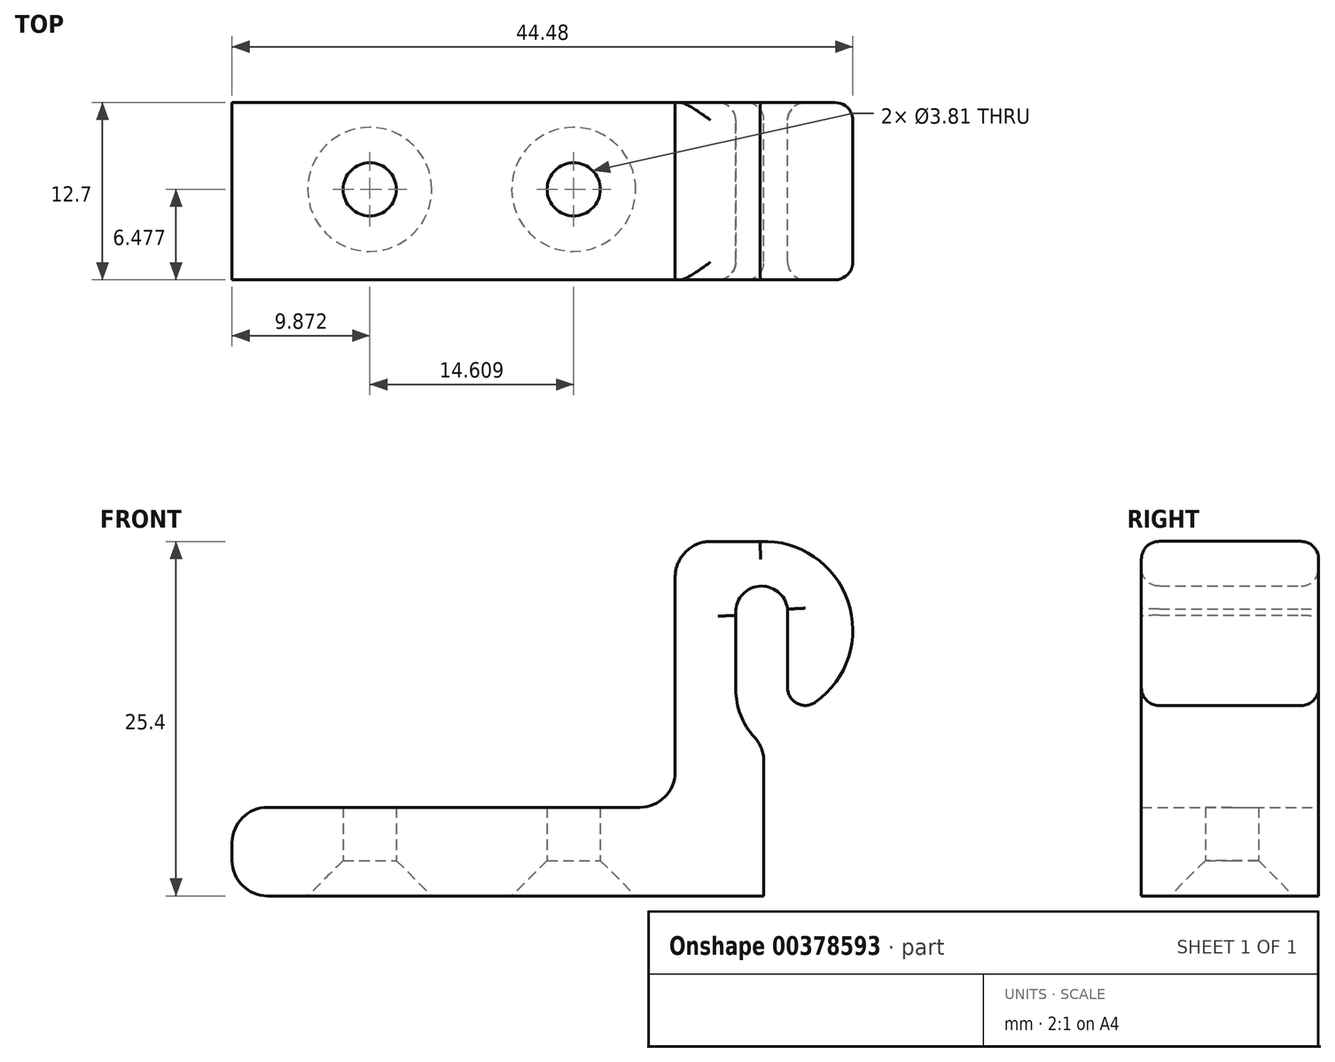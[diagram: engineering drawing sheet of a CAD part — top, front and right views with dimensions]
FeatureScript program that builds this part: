
annotation { "Feature Type Name" : "Feature", "Feature Type Description" : "" }
export const myFeature = defineFeature(function(context is Context, id is Id, definition is map)
    precondition{}
    {
        {
            var Q0;
            Q0=qCreatedBy(makeId("Front.planeOp"),FACE);
            var sketch = newSketch(context, id + "F0", { "sketchPlane" : qUnion([Q0])});
            skLineSegment(sketch, "E0.bottom", {"start": v(-17.17, 1.34) * mm, "end": v(14.58, 1.34) * mm});
            skLineSegment(sketch, "E0.top", {"start": v(-17.17, -5.01) * mm, "end": v(20.93, -5.01) * mm});
            skLineSegment(sketch, "E0.left", {"start": v(-17.17, 1.34) * mm, "end": v(-17.17, -5.01) * mm});
            skLineSegment(sketch, "E0.right", {"start": v(20.93, 1.34) * mm, "end": v(20.93, -5.01) * mm});
            skLineSegment(sketch, "E1.bottom", {"start": v(14.58, 20.39) * mm, "end": v(20.93, 20.39) * mm});
            skLineSegment(sketch, "E1.top", {"start": v(14.58, -5.01) * mm, "end": v(20.93, -5.01) * mm});
            skLineSegment(sketch, "E1.left", {"start": v(14.58, 20.39) * mm, "end": v(14.58, 1.34) * mm});
            skLineSegment(sketch, "E1.right", {"start": v(20.93, 7.13) * mm, "end": v(20.93, -5.01) * mm});
            skArc(sketch, "E2", {"start": v(22.64, 7.92) * mm, "mid": v(27.23, 15.03) * mm, "end": v(20.67, 20.39) * mm});
            skLineSegment(sketch, "E3", {"start": v(22.64, 7.92) * mm, "end": v(22.64, 15.54) * mm});
            skLineSegment(sketch, "E4", {"start": v(18.92, 15.1) * mm, "end": v(18.92, 7.13) * mm});
            skLineSegment(sketch, "E5", {"start": v(18.92, 7.13) * mm, "end": v(20.96, 7.13) * mm});
            skArc(sketch, "E6", {"start": v(22.64, 15.54) * mm, "mid": v(20.56, 17.18) * mm, "end": v(18.92, 15.1) * mm});
            skSolve(sketch);
        }
        {
            var Q0;
            Q0=makeQuery(id+"F0.imprint","IMPRINT",FACE,{"disambiguationData":[TD([[makeQuery(id+"F0.imprint","IMPRINT",EDGE,{"derivedFrom":sQuery(id+"F0.wireOp",EDGE,"E0.bottom")}),-1.0]])]});
            extrude(context, id + "F1", {"entities" : qUnion([Q0]), "depth" : 12.7 * mm});
        }
        {
            var Q0;
            Q0=makeQuery(id+"F1.opExtrude","SWEPT_EDGE",EDGE,{"disambiguationData":[OSD([sQuery(id+"F0.wireOp",EDGE,"E0.bottom"),sQuery(id+"F0.wireOp",EDGE,"E1.left")])]});
            var Q1;
            Q1=makeQuery(id+"F1.opExtrude","SWEPT_EDGE",EDGE,{"disambiguationData":[OSD([sQuery(id+"F0.wireOp",EDGE,"E1.top"),sQuery(id+"F0.wireOp",EDGE,"E1.right")])]});
            var Q2;
            Q2=makeQuery(id+"F1.opExtrude","SWEPT_EDGE",EDGE,{"disambiguationData":[OSD([sQuery(id+"F0.wireOp",EDGE,"E0.bottom"),sQuery(id+"F0.wireOp",EDGE,"E0.left")])]});
            var Q3;
            Q3=makeQuery(id+"F1.opExtrude","SWEPT_EDGE",EDGE,{"disambiguationData":[OSD([sQuery(id+"F0.wireOp",EDGE,"E0.top"),sQuery(id+"F0.wireOp",EDGE,"E0.left")])]});
            var Q4;
            Q4=makeQuery(id+"F1.opExtrude","SWEPT_EDGE",EDGE,{"disambiguationData":[OSD([sQuery(id+"F0.wireOp",EDGE,"E1.bottom"),sQuery(id+"F0.wireOp",EDGE,"E1.left")])]});
            var Q5;
            Q5=makeQuery(id+"F1.opExtrude","SWEPT_EDGE",EDGE,{"disambiguationData":[OSD([sQuery(id+"F0.wireOp",EDGE,"E1.right"),sQuery(id+"F0.wireOp",EDGE,"E5")])]});
            fillet(context, id + "F2", {"entities" : qUnion([Q0, Q1, Q2, Q3, Q4, Q5]), "radius" : 2.54 * mm, "tangentPropagation" : true, "allowEdgeOverflow" : false});
        }
        {
            var Q0;
            Q0=makeQuery(id+"F2.opFillet","BLEND_EDGE",EDGE,{"blendedFrom":[makeQuery(id+"F1.opExtrude","SWEPT_EDGE",EDGE,{"disambiguationData":[OSD([sQuery(id+"F0.wireOp",EDGE,"E1.right"),sQuery(id+"F0.wireOp",EDGE,"E5")])]}),makeQuery(id+"F1.opExtrude","SWEPT_FACE",FACE,{"disambiguationData":[OSD([sQuery(id+"F0.wireOp",EDGE,"E4")])]})],"blendedInto":[makeQuery(id+"F1.opExtrude","SWEPT_FACE",FACE,{"disambiguationData":[OSD([sQuery(id+"F0.wireOp",EDGE,"E4")])]})]});
            fillet(context, id + "F3", {"entities" : qUnion([Q0]), "radius" : 5.08 * mm, "tangentPropagation" : true, "allowEdgeOverflow" : false});
        }
        {
            var Q0;
            Q0=makeQuery(id+"F1.opExtrude","SWEPT_EDGE",EDGE,{"disambiguationData":[OSD([sQuery(id+"F0.wireOp",EDGE,"E2"),sQuery(id+"F0.wireOp",EDGE,"E3")])]});
            fillet(context, id + "F4", {"entities" : qUnion([Q0]), "radius" : 1.27 * mm, "tangentPropagation" : true, "allowEdgeOverflow" : false});
        }
        {
            var Q0;
            Q0=makeQuery(id+"F1.opExtrude","CAP_EDGE",EDGE,{"disambiguationData":[OSD([sQuery(id+"F0.wireOp",EDGE,"E6")])],"isStart":false});
            var Q1;
            Q1=makeQuery(id+"F1.opExtrude","CAP_EDGE",EDGE,{"disambiguationData":[OSD([sQuery(id+"F0.wireOp",EDGE,"E4")])],"isStart":false});
            var Q2;
            {var subQ0=sQuery(id+"F0.wireOp",EDGE,"E3");var subQ1=sQuery(id+"F0.wireOp",EDGE,"E2");Q2=makeQuery(id+"F4.opFillet","BLEND_EDGE",EDGE,{"blendedFrom":[makeQuery(id+"F1.opExtrude","SWEPT_EDGE",EDGE,{"disambiguationData":[OSD([subQ1,subQ0])]}),makeQuery(id+"F1.opExtrude","CAP_FACE",FACE,{"disambiguationData":[OSD([sQuery(id+"F0.wireOp",EDGE,"E0.bottom"),sQuery(id+"F0.wireOp",EDGE,"E0.top"),sQuery(id+"F0.wireOp",EDGE,"E0.left"),sQuery(id+"F0.wireOp",EDGE,"E1.bottom"),sQuery(id+"F0.wireOp",EDGE,"E1.top"),sQuery(id+"F0.wireOp",EDGE,"E1.left"),sQuery(id+"F0.wireOp",EDGE,"E1.right"),subQ1,subQ0,sQuery(id+"F0.wireOp",EDGE,"E4"),sQuery(id+"F0.wireOp",EDGE,"E5"),sQuery(id+"F0.wireOp",EDGE,"E6")])],"isStart":false})],"blendedInto":[makeQuery(id+"F1.opExtrude","CAP_FACE",FACE,{"disambiguationData":[OSD([sQuery(id+"F0.wireOp",EDGE,"E0.bottom"),sQuery(id+"F0.wireOp",EDGE,"E0.top"),sQuery(id+"F0.wireOp",EDGE,"E0.left"),sQuery(id+"F0.wireOp",EDGE,"E1.bottom"),sQuery(id+"F0.wireOp",EDGE,"E1.top"),sQuery(id+"F0.wireOp",EDGE,"E1.left"),sQuery(id+"F0.wireOp",EDGE,"E1.right"),subQ1,subQ0,sQuery(id+"F0.wireOp",EDGE,"E4"),sQuery(id+"F0.wireOp",EDGE,"E5"),sQuery(id+"F0.wireOp",EDGE,"E6")])],"isStart":false})]});}
            var Q3;
            Q3=makeQuery(id+"F1.opExtrude","CAP_EDGE",EDGE,{"disambiguationData":[OSD([sQuery(id+"F0.wireOp",EDGE,"E6")])],"isStart":true});
            var Q4;
            Q4=makeQuery(id+"F1.opExtrude","CAP_EDGE",EDGE,{"disambiguationData":[OSD([sQuery(id+"F0.wireOp",EDGE,"E4")])],"isStart":true});
            var Q5;
            Q5=makeQuery(id+"F1.opExtrude","CAP_EDGE",EDGE,{"disambiguationData":[OSD([sQuery(id+"F0.wireOp",EDGE,"E2")])],"isStart":true});
            fillet(context, id + "F5", {"entities" : qUnion([Q0, Q1, Q2, Q3, Q4, Q5]), "radius" : 1.27 * mm, "tangentPropagation" : true, "allowEdgeOverflow" : false});
        }
        {
            var Q0;
            Q0=qCreatedBy(makeId("Top.planeOp"),FACE);
            cPlane(context, id + "F6", {"entities" : qUnion([Q0]), "cplaneType" : CPlaneType.OFFSET, "offset" : 5.08 * mm, "oppositeDirection" : true, "width" : 152.4 * mm, "height" : 152.4 * mm});
        }
        {
            var Q0;
            Q0=qCreatedBy(id+"F6.planeOp",FACE);
            var sketch = newSketch(context, id + "F7", { "sketchPlane" : qUnion([Q0])});
            skPoint(sketch, "E7", {"position": v(7.31, -6.22) * mm});
            skPoint(sketch, "E8", {"position": v(-7.3, -6.22) * mm});
            skSolve(sketch);
        }
        {
            var Q0;
            Q0=sQuery(id+"F7.wireOp",VERTEX,"E8");
            var Q1;
            Q1=sQuery(id+"F7.wireOp",VERTEX,"E7");
            var Q2;
            Q2=makeQuery(id+"F1.opExtrude","SWEPT_BODY",BODY,{"disambiguationData":[OSD([sQuery(id+"F0.wireOp",EDGE,"E0.bottom"),sQuery(id+"F0.wireOp",EDGE,"E0.top"),sQuery(id+"F0.wireOp",EDGE,"E0.left"),sQuery(id+"F0.wireOp",EDGE,"E1.bottom"),sQuery(id+"F0.wireOp",EDGE,"E1.top"),sQuery(id+"F0.wireOp",EDGE,"E1.left"),sQuery(id+"F0.wireOp",EDGE,"E1.right"),sQuery(id+"F0.wireOp",EDGE,"E2"),sQuery(id+"F0.wireOp",EDGE,"E3"),sQuery(id+"F0.wireOp",EDGE,"E4"),sQuery(id+"F0.wireOp",EDGE,"E5"),sQuery(id+"F0.wireOp",EDGE,"E6")])]});
            hole(context, id + "F8", {"style" : HoleStyle.C_SINK, "endStyle" : HoleEndStyle.THROUGH, "oppositeDirection" : true, "holeDiameter" : 3.8 * mm, "cSinkDiameter" : 8.9 * mm, "cSinkAngle" : 90 * degree, "isTappedThrough" : true, "tappedDepth" : 12.7 * mm, "tapClearance" : 3, "locations" : qUnion([Q0, Q1]), "scope" : qUnion([Q2])});
        }
    });
